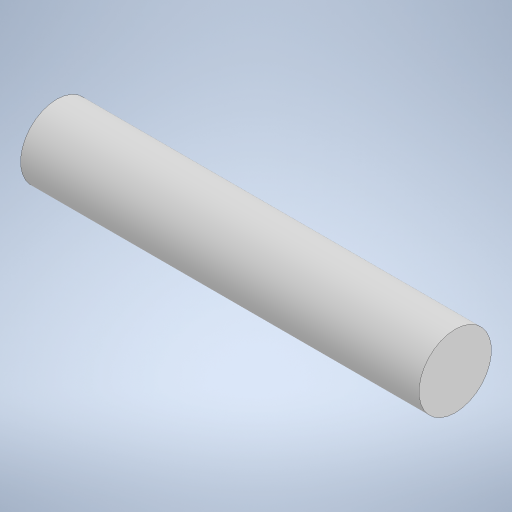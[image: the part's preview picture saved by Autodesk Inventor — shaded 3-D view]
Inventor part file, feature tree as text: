
AUTODESK INVENTOR PART (.ipt)
format: ipt  version: 2023 (Build 270158000, 158)  size: 216,576 bytes
history: native  units: mm
features: other x1, extrude x1, sketch x1
ambient origin geometry x8: Origin, YZ Plane, XZ Plane, XY Plane, X Axis, Y Axis, Z Axis, Center Point
bodies: Body1 (feature_tree)
feature tree (3):
  other  "Sólido1"
  extrude  "Extrusión1"  Depth=55.0mm TaperAngle=0.0deg
  sketch  "Boceto1"  dims[d0=10.0mm d1=55.0mm d2=0.0mm]
